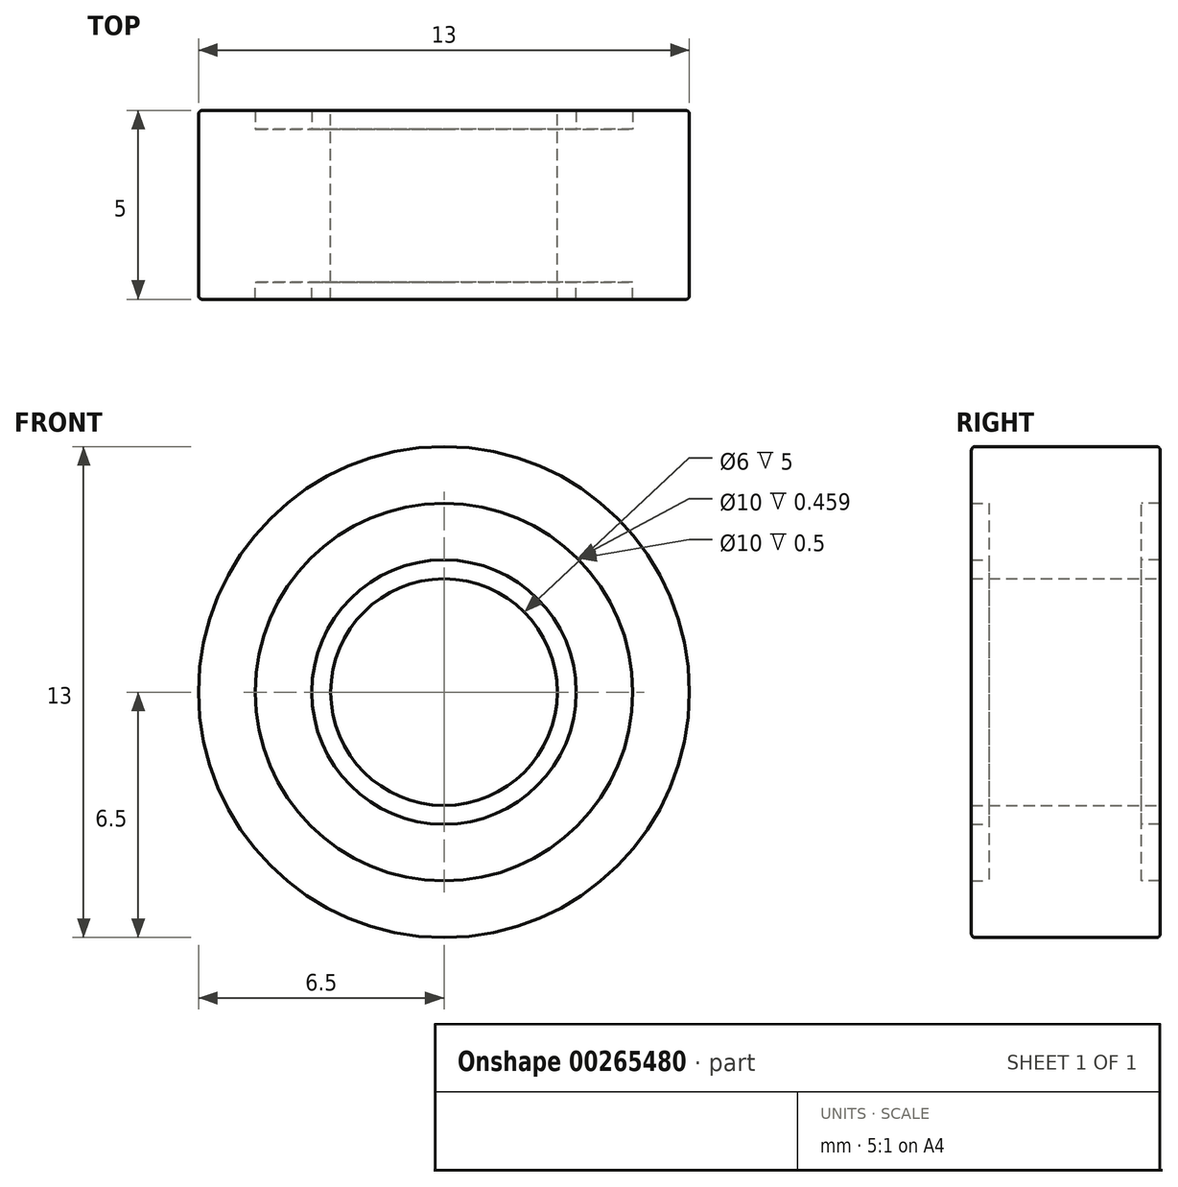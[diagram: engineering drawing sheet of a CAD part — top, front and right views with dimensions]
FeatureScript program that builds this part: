
annotation { "Feature Type Name" : "Feature", "Feature Type Description" : "" }
export const myFeature = defineFeature(function(context is Context, id is Id, definition is map)
    precondition{}
    {
        {
            var Q0;
            Q0=qCreatedBy(makeId("Front.planeOp"),FACE);
            var sketch = newSketch(context, id + "F0", { "sketchPlane" : qUnion([Q0])});
            skCircle(sketch, "E0", {"center": v(0, 0) * mm, "radius": 6.5 * mm});
            skCircle(sketch, "E1", {"center": v(0, 0) * mm, "radius": 3 * mm});
            skSolve(sketch);
        }
        {
            var Q0;
            Q0=makeQuery(id+"F0.imprint","IMPRINT",FACE,{"disambiguationData":[TD([[makeQuery(id+"F0.imprint","IMPRINT",EDGE,{"derivedFrom":sQuery(id+"F0.wireOp",EDGE,"E0")}),1.0]])]});
            extrude(context, id + "F1", {"entities" : qUnion([Q0]), "depth" : 5 * mm});
        }
        {
            var Q0;
            Q0=qCreatedBy(makeId("Top.planeOp"),FACE);
            var sketch = newSketch(context, id + "F2", { "sketchPlane" : qUnion([Q0])});
            skLineSegment(sketch, "E2", {"start": v(0, 0) * mm, "end": v(-3.5, 0) * mm});
            skLineSegment(sketch, "E3.bottom", {"start": v(-3.5, 0) * mm, "end": v(-5, 0) * mm});
            skLineSegment(sketch, "E3.top", {"start": v(-3.5, -0.5) * mm, "end": v(-5, -0.5) * mm});
            skLineSegment(sketch, "E3.left", {"start": v(-3.5, 0) * mm, "end": v(-3.5, -0.5) * mm});
            skLineSegment(sketch, "E3.right", {"start": v(-5, 0) * mm, "end": v(-5, -0.5) * mm});
            skLineSegment(sketch, "E4", {"start": v(0, 9.95) * mm, "end": v(0, -12.19) * mm, "construction": true});
            skLineSegment(sketch, "E5", {"start": v(0, -5.04) * mm, "end": v(-3.5, -5.04) * mm});
            skLineSegment(sketch, "E6.bottom", {"start": v(-3.5, -5.04) * mm, "end": v(-5, -5.04) * mm});
            skLineSegment(sketch, "E6.top", {"start": v(-3.5, -4.54) * mm, "end": v(-5, -4.54) * mm});
            skLineSegment(sketch, "E6.left", {"start": v(-3.5, -5.04) * mm, "end": v(-3.5, -4.54) * mm});
            skLineSegment(sketch, "E6.right", {"start": v(-5, -5.04) * mm, "end": v(-5, -4.54) * mm});
            skSolve(sketch);
        }
        {
            var Q0;
            Q0=makeQuery(id+"F2.imprint","IMPRINT",FACE,{"disambiguationData":[TD([[makeQuery(id+"F2.imprint","IMPRINT",EDGE,{"derivedFrom":sQuery(id+"F2.wireOp",EDGE,"E6.bottom")}),-1.0]])]});
            var Q1;
            Q1=sQuery(id+"F2.wireOp",EDGE,"E4");
            revolve(context, id + "F3", {"operationType" : NewBodyOperationType.REMOVE, "entities" : qUnion([Q0]), "axis" : qUnion([Q1]), "revolveType" : RevolveType.FULL});
        }
        {
            var Q0;
            Q0=makeQuery(id+"F2.imprint","IMPRINT",FACE,{"disambiguationData":[TD([[makeQuery(id+"F2.imprint","IMPRINT",EDGE,{"derivedFrom":sQuery(id+"F2.wireOp",EDGE,"E3.bottom")}),1.0]])]});
            var Q1;
            Q1=sQuery(id+"F2.wireOp",EDGE,"E4");
            revolve(context, id + "F4", {"operationType" : NewBodyOperationType.REMOVE, "entities" : qUnion([Q0]), "axis" : qUnion([Q1]), "revolveType" : RevolveType.FULL, "oppositeDirection" : true});
        }
        {
            var Q0;
            Q0=makeQuery(id+"F1.opExtrude","CAP_EDGE",EDGE,{"disambiguationData":[OSD([sQuery(id+"F0.wireOp",EDGE,"E0")])],"isStart":false});
            fillet(context, id + "F5", {"entities" : qUnion([Q0]), "radius" : 0.1 * mm, "tangentPropagation" : true, "allowEdgeOverflow" : false});
        }
        {
            var Q0;
            Q0=makeQuery(id+"F1.opExtrude","CAP_EDGE",EDGE,{"disambiguationData":[OSD([sQuery(id+"F0.wireOp",EDGE,"E0")])],"isStart":true});
            fillet(context, id + "F6", {"entities" : qUnion([Q0]), "radius" : 0.1 * mm, "tangentPropagation" : true, "allowEdgeOverflow" : false});
        }
    });
